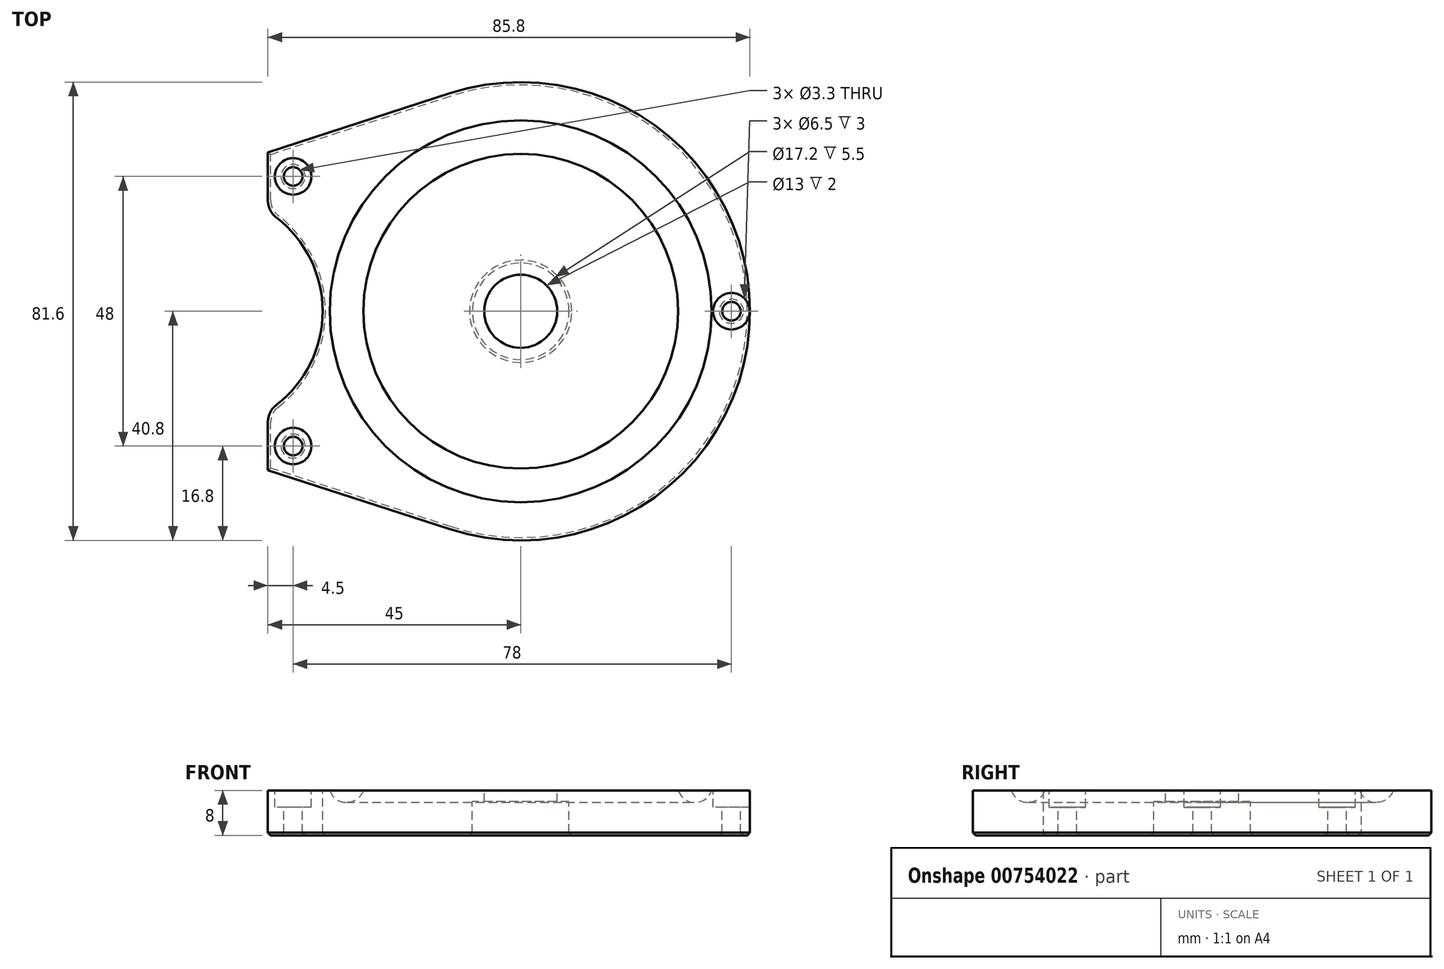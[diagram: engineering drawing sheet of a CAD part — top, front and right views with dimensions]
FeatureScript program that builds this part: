
annotation { "Feature Type Name" : "Feature", "Feature Type Description" : "" }
export const myFeature = defineFeature(function(context is Context, id is Id, definition is map)
    precondition{}
    {
        {
            var Q0;
            Q0=qCreatedBy(makeId("Top.planeOp"),FACE);
            var sketch = newSketch(context, id + "F0", { "sketchPlane" : qUnion([Q0])});
            skCircle(sketch, "E0", {"center": v(0, 0) * mm, "radius": 40.8 * mm});
            skSolve(sketch);
        }
        {
            var Q0;
            Q0=qSketchRegion(id+"F0",true);
            extrude(context, id + "F1", {"entities" : qUnion([Q0]), "depth" : 8 * mm});
        }
        {
            var Q0;
            Q0=qCreatedBy(makeId("Right.planeOp"),FACE);
            var sketch = newSketch(context, id + "F2", { "sketchPlane" : qUnion([Q0])});
            skLineSegment(sketch, "E1", {"start": v(0, 0) * mm, "end": v(0, 8) * mm});
            skLineSegment(sketch, "E2", {"start": v(0, 8) * mm, "end": v(6.5, 8) * mm});
            skLineSegment(sketch, "E3", {"start": v(6.5, 8) * mm, "end": v(6.5, 6) * mm});
            skLineSegment(sketch, "E4", {"start": v(6.5, 6) * mm, "end": v(8.6, 6) * mm});
            skLineSegment(sketch, "E5", {"start": v(8.6, 6) * mm, "end": v(8.6, 0) * mm});
            skLineSegment(sketch, "E6", {"start": v(8.6, 0) * mm, "end": v(0, 0) * mm});
            skLineSegment(sketch, "E7", {"start": v(0, 8) * mm, "end": v(0, 13.47) * mm, "construction": true});
            skSolve(sketch);
        }
        {
            var Q0;
            Q0=qSketchRegion(id+"F2",true);
            var Q1;
            Q1=sQuery(id+"F2.wireOp",EDGE,"E7");
            revolve(context, id + "F3", {"operationType" : NewBodyOperationType.REMOVE, "entities" : qUnion([Q0]), "axis" : qUnion([Q1]), "revolveType" : RevolveType.FULL, "oppositeDirection" : true});
        }
        {
            var Q0;
            Q0=qCreatedBy(makeId("Right.planeOp"),FACE);
            var sketch = newSketch(context, id + "F4", { "sketchPlane" : qUnion([Q0])});
            skCircle(sketch, "E8", {"center": v(31, 9) * mm, "radius": 3.15 * mm});
            skLineSegment(sketch, "E9", {"start": v(0, -0.8) * mm, "end": v(0, 13.57) * mm, "construction": true});
            skSolve(sketch);
        }
        {
            var Q0;
            Q0=qSketchRegion(id+"F4",true);
            var Q1;
            Q1=sQuery(id+"F4.wireOp",EDGE,"E9");
            revolve(context, id + "F5", {"operationType" : NewBodyOperationType.REMOVE, "entities" : qUnion([Q0]), "axis" : qUnion([Q1]), "revolveType" : RevolveType.FULL, "oppositeDirection" : true});
        }
        {
            var Q0;
            Q0=qCreatedBy(makeId("Top.planeOp"),FACE);
            var sketch = newSketch(context, id + "F6", { "sketchPlane" : qUnion([Q0])});
            skLineSegment(sketch, "E10.bottom", {"start": v(-36, 19.2) * mm, "end": v(-40.8, 19.2) * mm});
            skLineSegment(sketch, "E10.top", {"start": v(-36, -19.2) * mm, "end": v(-40.8, -19.2) * mm});
            skLineSegment(sketch, "E10.left", {"start": v(-36, 19.2) * mm, "end": v(-36, -19.2) * mm});
            skLineSegment(sketch, "E10.right", {"start": v(-40.8, 19.2) * mm, "end": v(-40.8, -19.2) * mm});
            skSolve(sketch);
        }
        {
            var Q0;
            Q0=qSketchRegion(id+"F6",true);
            extrude(context, id + "F7", {"entities" : qUnion([Q0]), "operationType" : NewBodyOperationType.REMOVE, "endBound" : BoundingType.THROUGH_ALL, "depth" : 25 * mm});
        }
        {
            var Q0;
            Q0=qCreatedBy(makeId("Top.planeOp"),FACE);
            var sketch = newSketch(context, id + "F8", { "sketchPlane" : qUnion([Q0])});
            skLineSegment(sketch, "E11", {"start": v(-45, -28.28) * mm, "end": v(-45, 28.28) * mm});
            skLineSegment(sketch, "E12", {"start": v(-45, 28.28) * mm, "end": v(-12.6, 38.8) * mm});
            skLineSegment(sketch, "E13", {"start": v(0, 0) * mm, "end": v(-51.86, 0) * mm, "construction": true});
            skArc(sketch, "E14.0", {"start": v(-12.6, 38.8) * mm, "mid": v(-26.2, 31.27) * mm, "end": v(-36, 19.2) * mm});
            skPoint(sketch, "E15.orphan", {"position": v(-36, -19.2) * mm});
            skLineSegment(sketch, "E16.MirrorCS", {"start": v(-45, -28.28) * mm, "end": v(-12.6, -38.8) * mm});
            skArc(sketch, "E17.MirrorCS", {"start": v(-12.6, -38.8) * mm, "mid": v(-26.2, -31.27) * mm, "end": v(-36, -19.2) * mm});
            skLineSegment(sketch, "E18", {"start": v(-36, 19.2) * mm, "end": v(-36, -19.2) * mm});
            skSolve(sketch);
        }
        {
            var Q0;
            Q0=qSketchRegion(id+"F8",true);
            var Q1;
            {var subQ0=sQuery(id+"F0.wireOp",EDGE,"E0");Q1=makeQuery(id+"F5.boolean.opBoolean","SPLIT",FACE,{"disambiguationData":[TD([makeQuery(id+"F1.opExtrude","SWEPT_FACE",FACE,{"disambiguationData":[OSD([subQ0])]})])],"derivedFrom":makeQuery(id+"F1.opExtrude","CAP_FACE",FACE,{"disambiguationData":[OSD([subQ0])],"isStart":false})});}
            extrude(context, id + "F9", {"entities" : qUnion([Q0]), "operationType" : NewBodyOperationType.ADD, "endBound" : BoundingType.UP_TO_SURFACE, "endBoundEntityFace" : qUnion([Q1]), "depth" : 25 * mm});
        }
        {
            var Q0;
            {var subQ0=sQuery(id+"F0.wireOp",EDGE,"E0");Q0=makeQuery(id+"F9.boolean.opBoolean","MERGE",FACE,{"derivedFrom":[makeQuery(id+"F5.boolean.opBoolean","SPLIT",FACE,{"disambiguationData":[TD([makeQuery(id+"F1.opExtrude","SWEPT_FACE",FACE,{"disambiguationData":[OSD([subQ0])]})])],"derivedFrom":makeQuery(id+"F1.opExtrude","CAP_FACE",FACE,{"disambiguationData":[OSD([subQ0])],"isStart":false})}),makeQuery(id+"F9.opExtrude","CAP_FACE",FACE,{"disambiguationData":[OSD([sQuery(id+"F8.wireOp",EDGE,"E11"),sQuery(id+"F8.wireOp",EDGE,"E12"),sQuery(id+"F8.wireOp",EDGE,"E14.0"),sQuery(id+"F8.wireOp",EDGE,"E16.MirrorCS"),sQuery(id+"F8.wireOp",EDGE,"E17.MirrorCS"),sQuery(id+"F8.wireOp",EDGE,"E18")])],"isStart":false})]});}
            var sketch = newSketch(context, id + "F10", { "sketchPlane" : qUnion([Q0])});
            skCircle(sketch, "E19", {"center": v(-56.25, 0) * mm, "radius": 21 * mm});
            skLineSegment(sketch, "E20", {"start": v(-56.25, 0) * mm, "end": v(0, 0) * mm, "construction": true});
            skSolve(sketch);
        }
        {
            var Q0;
            Q0=qSketchRegion(id+"F10",true);
            extrude(context, id + "F11", {"entities" : qUnion([Q0]), "operationType" : NewBodyOperationType.REMOVE, "endBound" : BoundingType.THROUGH_ALL, "oppositeDirection" : true, "depth" : 25 * mm});
        }
        {
            var Q0;
            Q0=makeQuery(id+"F11.boolean.opBoolean","INTERSECT",EDGE,{"disambiguationData":[OD(1.0)],"derivedFrom":[makeQuery(id+"F9.opExtrude","SWEPT_FACE",FACE,{"disambiguationData":[OSD([sQuery(id+"F8.wireOp",EDGE,"E11")])]}),makeQuery(id+"F11.opExtrude","SWEPT_FACE",FACE,{"disambiguationData":[OSD([sQuery(id+"F10.wireOp",EDGE,"E19")])]})]});
            var Q1;
            Q1=makeQuery(id+"F11.boolean.opBoolean","INTERSECT",EDGE,{"disambiguationData":[OD(0.0)],"derivedFrom":[makeQuery(id+"F9.opExtrude","SWEPT_FACE",FACE,{"disambiguationData":[OSD([sQuery(id+"F8.wireOp",EDGE,"E11")])]}),makeQuery(id+"F11.opExtrude","SWEPT_FACE",FACE,{"disambiguationData":[OSD([sQuery(id+"F10.wireOp",EDGE,"E19")])]})]});
            fillet(context, id + "F12", {"entities" : qUnion([Q0, Q1]), "radius" : 4 * mm, "tangentPropagation" : true, "allowEdgeOverflow" : false});
        }
        {
            var Q0;
            {var subQ0=sQuery(id+"F0.wireOp",EDGE,"E0");Q0=makeQuery(id+"F9.boolean.opBoolean","MERGE",FACE,{"derivedFrom":[makeQuery(id+"F5.boolean.opBoolean","SPLIT",FACE,{"disambiguationData":[TD([makeQuery(id+"F1.opExtrude","SWEPT_FACE",FACE,{"disambiguationData":[OSD([subQ0])]})])],"derivedFrom":makeQuery(id+"F1.opExtrude","CAP_FACE",FACE,{"disambiguationData":[OSD([subQ0])],"isStart":false})}),makeQuery(id+"F9.opExtrude","CAP_FACE",FACE,{"disambiguationData":[OSD([sQuery(id+"F8.wireOp",EDGE,"E11"),sQuery(id+"F8.wireOp",EDGE,"E12"),sQuery(id+"F8.wireOp",EDGE,"E14.0"),sQuery(id+"F8.wireOp",EDGE,"E16.MirrorCS"),sQuery(id+"F8.wireOp",EDGE,"E17.MirrorCS"),sQuery(id+"F8.wireOp",EDGE,"E18")])],"isStart":false})]});}
            var sketch = newSketch(context, id + "F13", { "sketchPlane" : qUnion([Q0])});
            skPoint(sketch, "E21", {"position": v(-40.5, 24) * mm});
            skPoint(sketch, "E22", {"position": v(37.5, 0) * mm});
            skLineSegment(sketch, "E23", {"start": v(0, 0) * mm, "end": v(47.97, 0) * mm, "construction": true});
            skPoint(sketch, "E24.MirrorP", {"position": v(-40.5, -24) * mm});
            skSolve(sketch);
        }
        {
            var Q0;
            Q0=sQuery(id+"F13.wireOp",VERTEX,"E21");
            var Q1;
            Q1=sQuery(id+"F13.wireOp",VERTEX,"E24.MirrorP");
            var Q2;
            Q2=sQuery(id+"F13.wireOp",VERTEX,"E22");
            var Q3;
            Q3=makeQuery(id+"F1.opExtrude","SWEPT_BODY",BODY,{"disambiguationData":[OSD([sQuery(id+"F0.wireOp",EDGE,"E0")])]});
            hole(context, id + "F14", {"style" : HoleStyle.C_BORE, "endStyle" : HoleEndStyle.THROUGH, "standardTappedOrClearance" : lookupTablePath({ "standard" : "ISO", "fit" : "Normal", "size" : "M3", "type" : "Clearance" }), "standardBlindInLast" : lookupTablePath({ "fit" : "Standard", "standard" : "ISO", "size" : "M3", "type" : "Clearance" }), "holeDiameter" : 3.3 * mm, "cBoreDiameter" : 6.5 * mm, "cBoreDepth" : 3 * mm, "tappedDepth" : 12 * mm, "tapClearance" : 3, "locations" : qUnion([Q0, Q1, Q2]), "scope" : qUnion([Q3])});
        }
        {
            var Q0;
            Q0=makeQuery(id+"F9.boolean.opBoolean","MERGE",FACE,{"derivedFrom":[makeQuery(id+"F1.opExtrude","CAP_FACE",FACE,{"disambiguationData":[OSD([sQuery(id+"F0.wireOp",EDGE,"E0")])],"isStart":true}),makeQuery(id+"F9.opExtrude","CAP_FACE",FACE,{"disambiguationData":[OSD([sQuery(id+"F8.wireOp",EDGE,"E11"),sQuery(id+"F8.wireOp",EDGE,"E12"),sQuery(id+"F8.wireOp",EDGE,"E14.0"),sQuery(id+"F8.wireOp",EDGE,"E16.MirrorCS"),sQuery(id+"F8.wireOp",EDGE,"E17.MirrorCS"),sQuery(id+"F8.wireOp",EDGE,"E18")])],"isStart":true})]});
            chamfer(context, id + "F15", {"entities" : qUnion([Q0]), "width" : .5 * mm, "tangentPropagation" : true});
        }
    });
